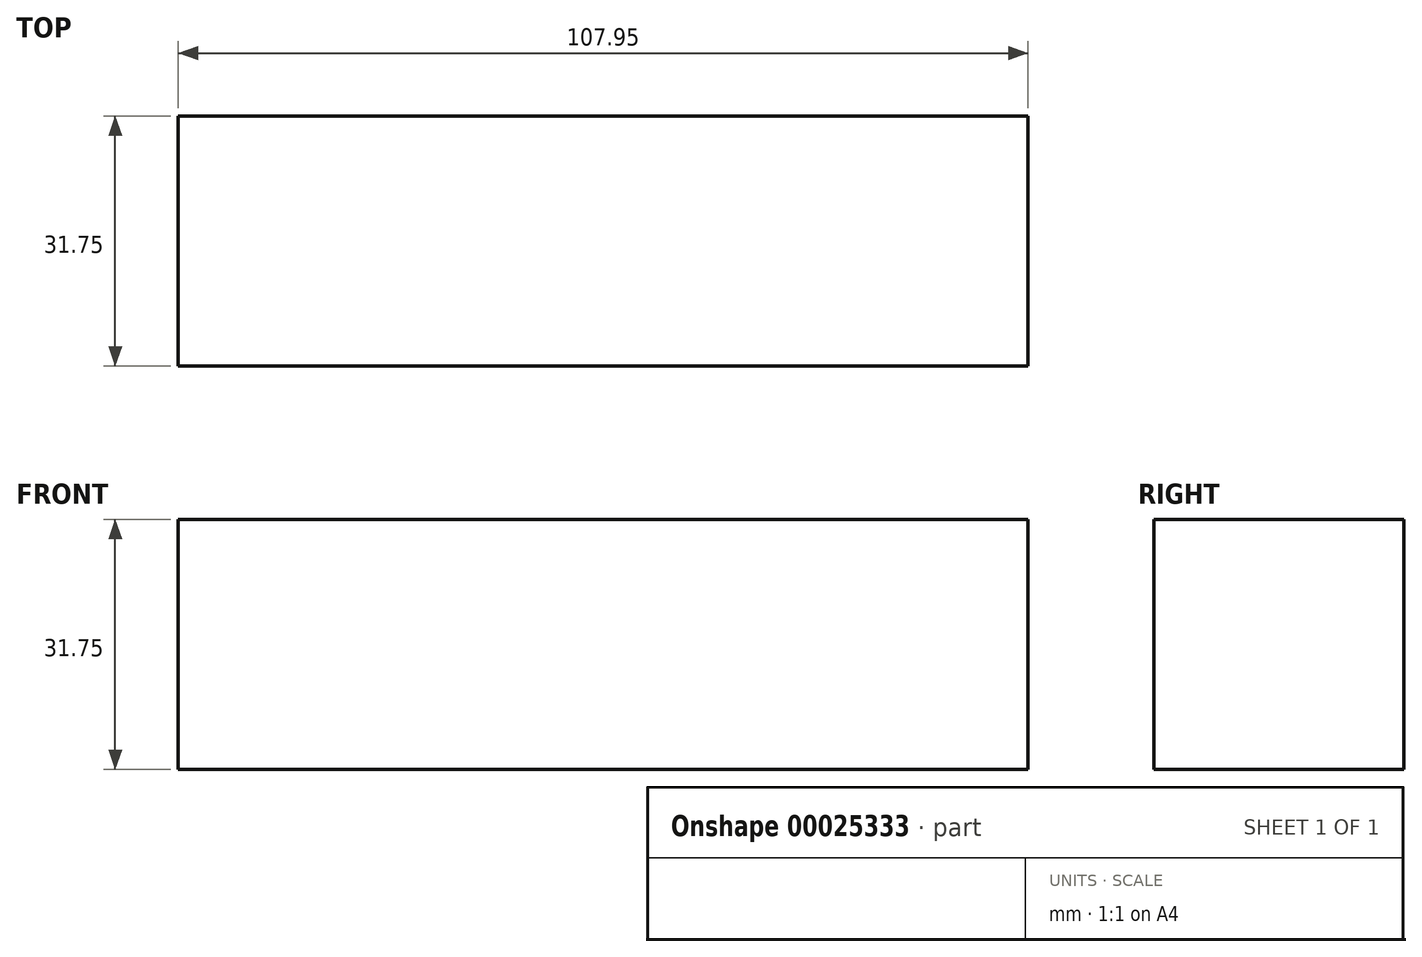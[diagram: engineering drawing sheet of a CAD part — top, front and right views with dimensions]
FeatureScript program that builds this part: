
annotation { "Feature Type Name" : "Feature", "Feature Type Description" : "" }
export const myFeature = defineFeature(function(context is Context, id is Id, definition is map)
    precondition{}
    {
        {
            var Q0;
            Q0=qCreatedBy(makeId("Front.planeOp"),FACE);
            var sketch = newSketch(context, id + "F0", { "sketchPlane" : qUnion([Q0])});
            skLineSegment(sketch, "E0.bottom", {"start": v(-44.58, 3.66) * mm, "end": v(63.37, 3.66) * mm});
            skLineSegment(sketch, "E0.top", {"start": v(-44.58, -28.09) * mm, "end": v(63.37, -28.09) * mm});
            skLineSegment(sketch, "E0.left", {"start": v(-44.58, 3.66) * mm, "end": v(-44.58, -28.09) * mm});
            skLineSegment(sketch, "E0.right", {"start": v(63.37, 3.66) * mm, "end": v(63.37, -28.09) * mm});
            skSolve(sketch);
        }
        {
            var Q0;
            Q0=makeQuery(id+"F0.imprint","IMPRINT",FACE,{"disambiguationData":[TD([[makeQuery(id+"F0.imprint","IMPRINT",EDGE,{"derivedFrom":sQuery(id+"F0.wireOp",EDGE,"E0.bottom")}),-1.0]])]});
            extrude(context, id + "F1", {"entities" : qUnion([Q0]), "depth" : 31.75 * mm});
        }
    });
